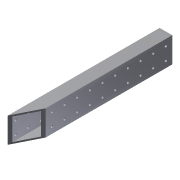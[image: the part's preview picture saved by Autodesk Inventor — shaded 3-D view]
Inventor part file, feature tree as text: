
AUTODESK INVENTOR PART (.ipt)
format: ipt  version: 2012 (Build 160160000, 160)  size: 139,264 bytes
history: native  units: in
note: dims shown in document units (in); Inventor stores cm internally (conversion verified against a paired STEP export)
features: extrude x3, sketch x3, shell x1, pattern_linear x1
ambient origin geometry x8: Origin, YZ Plane, XZ Plane, XY Plane, X Axis, Y Axis, Z Axis, Center Point
bodies: Solid1 (feature_tree)
feature tree (8):
  extrude  "Extrusion1"  Depth=2.0in
  shell  "Shell1"  Thickness=12.0in
  extrude  "Extrusion2"  Depth=0.1875in
  pattern_linear  "Rectangular Pattern1"  Spacing1=0.5in  [1 undecoded]
  extrude  "Extrusion3"  Depth=12.0in TaperAngle=0.0deg
  sketch  "Sketch1"  dims[d0=1.0in d1=2.0in d2=12.0in d3=0.0in]
  sketch  "Sketch2"  dims[d4=0.125in d5=0.1875in]
  sketch  "Sketch3"  dims[d6=0.5in d7=0.5in d8=12.0in d9=0.0in d10=4.7244in d12=1.0in d13=0.7874in d15=1.0in d16=2.0in d17=12.0in d18=0.0in]
note: 1 required parameter value undecoded (feature->parameter linkage not recoverable at this tier; creation-order binding heuristic only, values carry confidence <= 0.55)
